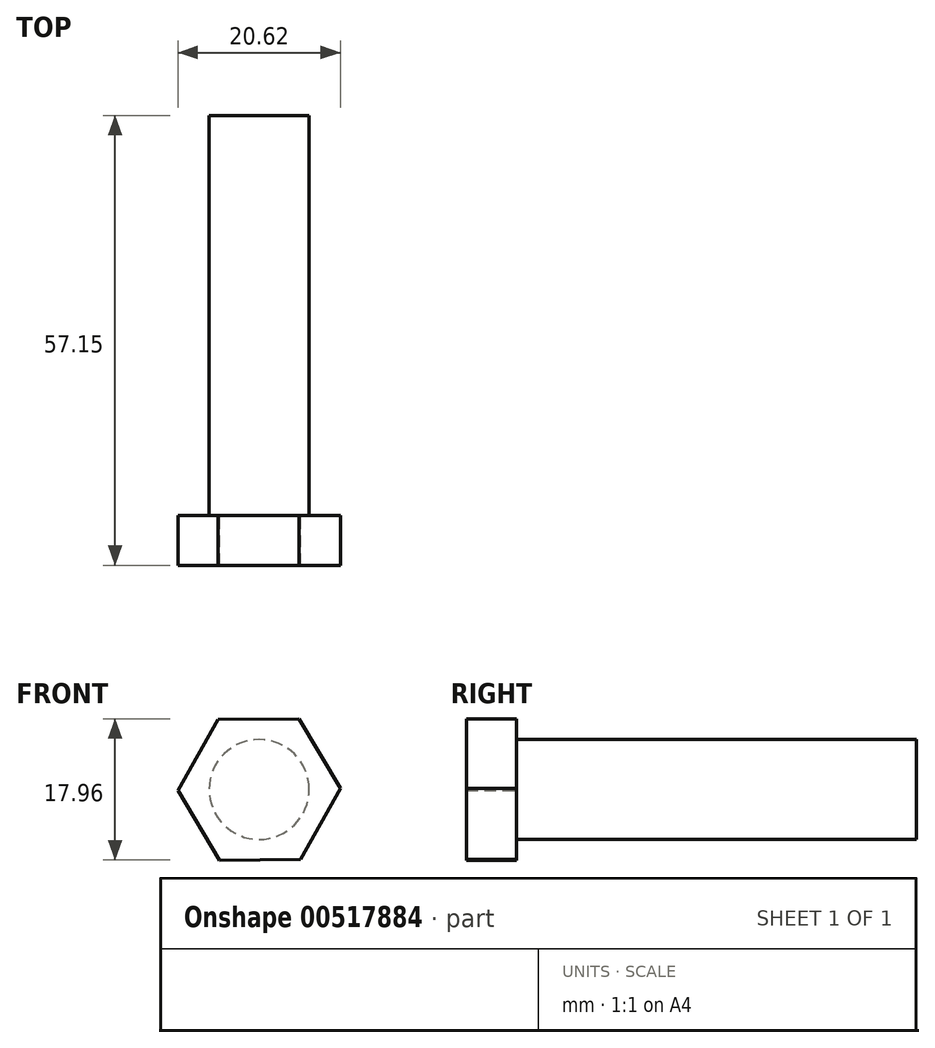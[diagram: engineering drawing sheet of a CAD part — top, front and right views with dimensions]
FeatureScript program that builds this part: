
annotation { "Feature Type Name" : "Feature", "Feature Type Description" : "" }
export const myFeature = defineFeature(function(context is Context, id is Id, definition is map)
    precondition{}
    {
        {
            var Q0;
            Q0=qCreatedBy(makeId("Front.planeOp"),FACE);
            var sketch = newSketch(context, id + "F0", { "sketchPlane" : qUnion([Q0])});
            skCircle(sketch, "E0", {"center": v(0, 0) * mm, "radius": 6.35 * mm});
            skSolve(sketch);
        }
        {
            var Q0;
            Q0=makeQuery(id+"F0.imprint","IMPRINT",FACE,{"disambiguationData":[TD([[makeQuery(id+"F0.imprint","IMPRINT",EDGE,{"derivedFrom":sQuery(id+"F0.wireOp",EDGE,"E0")}),1.0]])]});
            extrude(context, id + "F1", {"entities" : qUnion([Q0]), "oppositeDirection" : true, "depth" : 50.8 * mm, "offsetDistance" : 25.4 * mm});
        }
        {
            var Q0;
            Q0=makeQuery(id+"F1.opExtrude","CAP_FACE",FACE,{"disambiguationData":[OSD([sQuery(id+"F0.wireOp",EDGE,"E0")])],"isStart":true});
            var sketch = newSketch(context, id + "F2", { "sketchPlane" : qUnion([Q0])});
            skCircle(sketch, "E1.cCircle", {"center": v(0, 0) * mm, "radius": 8.93 * mm, "construction": true});
            skLineSegment(sketch, "E1.0", {"start": v(5.05, 8.98) * mm, "end": v(10.3, 0.12) * mm});
            skLineSegment(sketch, "E1.1", {"start": v(10.3, 0.12) * mm, "end": v(5.25, -8.87) * mm});
            skLineSegment(sketch, "E1.2", {"start": v(5.25, -8.87) * mm, "end": v(-5.05, -8.98) * mm});
            skLineSegment(sketch, "E1.3", {"start": v(-5.05, -8.98) * mm, "end": v(-10.3, -0.12) * mm});
            skLineSegment(sketch, "E1.4", {"start": v(-10.3, -0.12) * mm, "end": v(-5.25, 8.87) * mm});
            skLineSegment(sketch, "E1.5", {"start": v(-5.25, 8.87) * mm, "end": v(5.05, 8.98) * mm});
            skPoint(sketch, "E1.0.midPoint", {"position": v(7.68, 4.55) * mm});
            skSolve(sketch);
        }
        {
            var Q0;
            Q0=makeQuery(id+"F2.imprint","IMPRINT",FACE,{"disambiguationData":[TD([[makeQuery(id+"F2.imprint","IMPRINT",EDGE,{"derivedFrom":sQuery(id+"F2.wireOp",EDGE,"E1.0")}),-1.0]])]});
            var Q1;
            Q1=makeQuery(id+"F2.imprint","IMPRINT",FACE,{"disambiguationData":[TD([[makeQuery(id+"F2.imprint","IMPRINT",EDGE,{"derivedFrom":makeQuery(id+"F1.opExtrude","CAP_EDGE",EDGE,{"disambiguationData":[OSD([sQuery(id+"F0.wireOp",EDGE,"E0")])],"isStart":true})}),1.0]])]});
            extrude(context, id + "F3", {"entities" : qUnion([Q0, Q1]), "operationType" : NewBodyOperationType.ADD, "depth" : 6.35 * mm, "offsetDistance" : 25.4 * mm});
        }
    });
